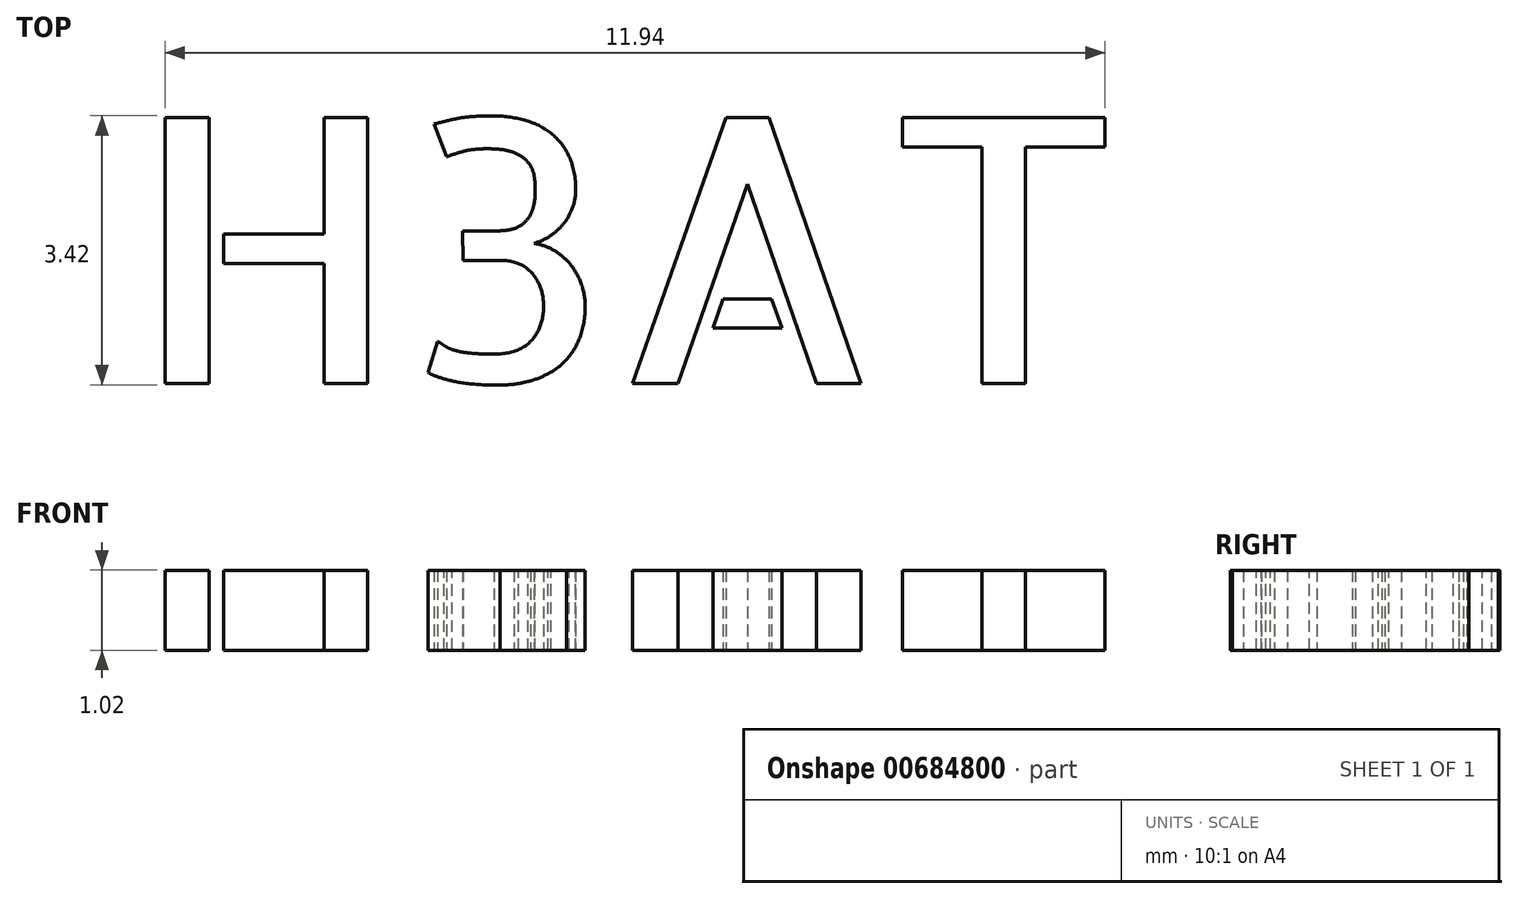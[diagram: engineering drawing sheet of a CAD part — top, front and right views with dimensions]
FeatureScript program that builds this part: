
annotation { "Feature Type Name" : "Feature", "Feature Type Description" : "" }
export const myFeature = defineFeature(function(context is Context, id is Id, definition is map)
    precondition{}
    {
        {
            var Q0;
            Q0=qCreatedBy(makeId("Top.planeOp"),FACE);
            var sketch = newSketch(context, id + "F0", { "sketchPlane" : qUnion([Q0])});
            skText(sketch, "E0", { "text": "H3AT", "fontName": "AllertaStencil-Regular.ttf"});
            const initialGuessF0  = {"E0": [-0.00625, -0.00173, 1, 0, 0.00338]};
            skSetInitialGuess(sketch, initialGuessF0);
            skSolve(sketch);
        }
        {
            var Q0;
            Q0 = qSketchRegion(id + "F0", true);
            extrude(context, id + "F1", {"entities" : qUnion([Q0]), "depth" : 1.02 * mm, "offsetDistance" : 25.4 * mm});
        }
    });
